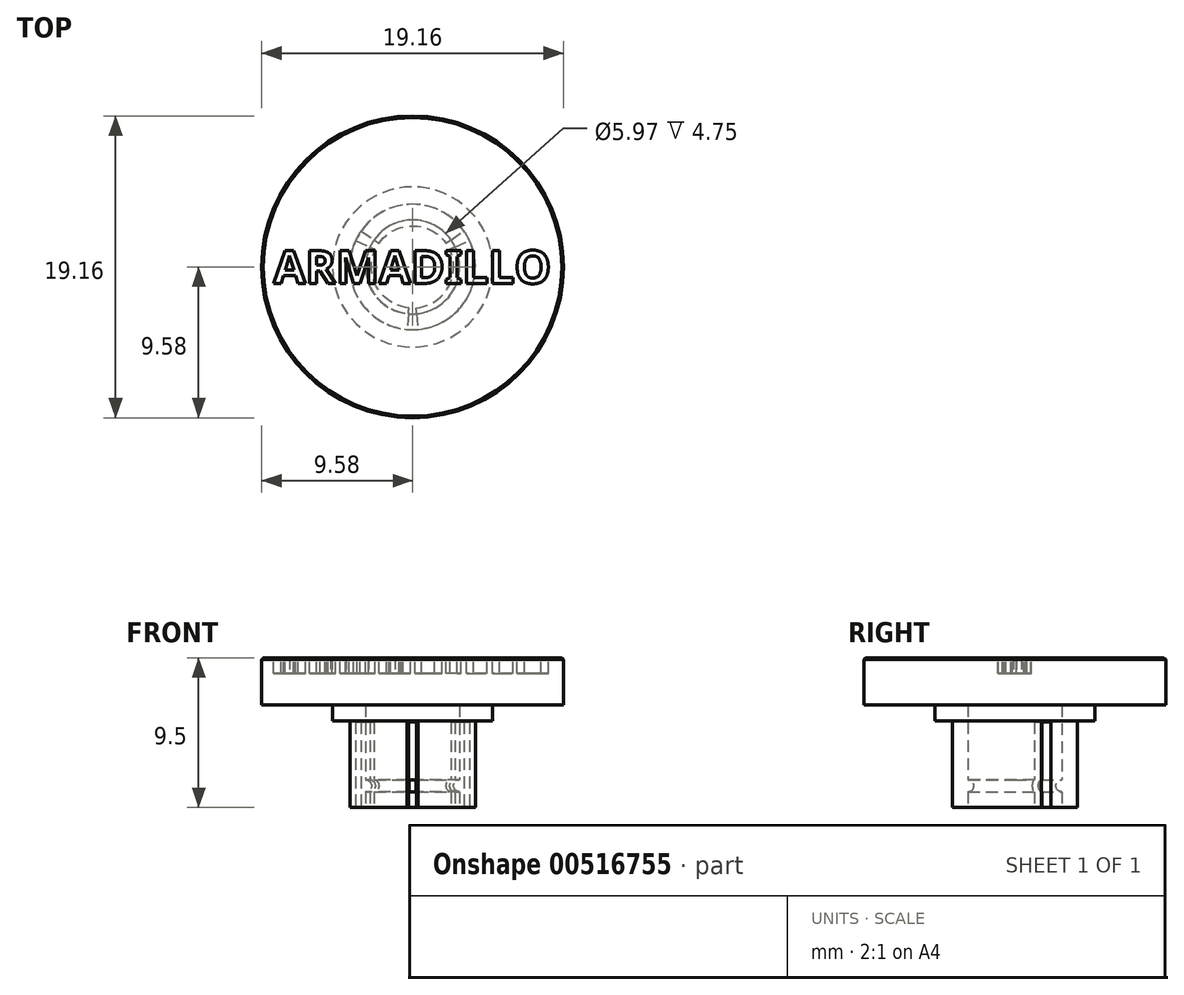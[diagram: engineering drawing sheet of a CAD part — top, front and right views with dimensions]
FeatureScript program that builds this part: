
annotation { "Feature Type Name" : "Feature", "Feature Type Description" : "" }
export const myFeature = defineFeature(function(context is Context, id is Id, definition is map)
    precondition{}
    {
        {
            var Q0;
            Q0=qCreatedBy(makeId("Front.planeOp"),FACE);
            var sketch = newSketch(context, id + "F0", { "sketchPlane" : qUnion([Q0])});
            skLineSegment(sketch, "E0", {"start": v(0, 6.5) * mm, "end": v(0, 9.5) * mm});
            skLineSegment(sketch, "E1", {"start": v(0, 9.5) * mm, "end": v(9.58, 9.5) * mm});
            skLineSegment(sketch, "E2", {"start": v(9.58, 9.5) * mm, "end": v(9.58, 6.5) * mm});
            skLineSegment(sketch, "E3", {"start": v(9.58, 6.5) * mm, "end": v(5.08, 6.5) * mm});
            skLineSegment(sketch, "E4", {"start": v(5.08, 6.5) * mm, "end": v(5.08, 5.5) * mm});
            skLineSegment(sketch, "E5", {"start": v(5.08, 5.5) * mm, "end": v(3.98, 5.5) * mm});
            skLineSegment(sketch, "E6", {"start": v(3.98, 5.5) * mm, "end": v(3.98, 0) * mm});
            skLineSegment(sketch, "E7", {"start": v(2.98, 6.5) * mm, "end": v(0, 6.5) * mm});
            skLineSegment(sketch, "E8", {"start": v(3.98, 0) * mm, "end": v(2.98, 0) * mm});
            skLineSegment(sketch, "E9", {"start": v(2.98, 0) * mm, "end": v(2.98, 1) * mm});
            skArc(sketch, "E10", {"start": v(2.98, 1.75) * mm, "mid": v(2.6, 1.37) * mm, "end": v(2.98, 1) * mm});
            skLineSegment(sketch, "E11.trimOffspring", {"start": v(2.98, 1.75) * mm, "end": v(2.98, 6.5) * mm});
            skSolve(sketch);
        }
        {
            var Q0;
            Q0=makeQuery(id+"F0.imprint","IMPRINT",FACE,{"disambiguationData":[TD([[makeQuery(id+"F0.imprint","IMPRINT",EDGE,{"derivedFrom":sQuery(id+"F0.wireOp",EDGE,"E0")}),-1.0]])]});
            var Q1;
            Q1=sQuery(id+"F0.wireOp",EDGE,"E0");
            revolve(context, id + "F1", {"entities" : qUnion([Q0]), "axis" : qUnion([Q1]), "revolveType" : RevolveType.FULL});
        }
        {
            var Q0;
            Q0=makeQuery(id+"F1.opRevolve","SWEPT_EDGE",EDGE,{"disambiguationData":[OSD([sQuery(id+"F0.wireOp",EDGE,"E1"),sQuery(id+"F0.wireOp",EDGE,"E2")])]});
            chamfer(context, id + "F2", {"entities" : qUnion([Q0]), "width" : 0.1 * mm, "tangentPropagation" : true});
        }
        {
            var Q0;
            Q0=makeQuery(id+"F1.opRevolve","SWEPT_FACE",FACE,{"disambiguationData":[OSD([sQuery(id+"F0.wireOp",EDGE,"E1")])]});
            var sketch = newSketch(context, id + "F3", { "sketchPlane" : qUnion([Q0])});
            skText(sketch, "E12", { "text": "ARMADILLO", "fontName": "NotoSans-Bold.ttf"});
            skPoint(sketch, "E13", {"position": v(0, 0) * mm});
            const initialGuessF3  = {"E12": [-0.00882, -0.00105, 1, 0, 0.0021]};
            skSetInitialGuess(sketch, initialGuessF3);
            skSolve(sketch);
        }
        {
            var Q0;
            Q0=qSketchRegion(id+"F3",true);
            extrude(context, id + "F4", {"entities" : qUnion([Q0]), "operationType" : NewBodyOperationType.REMOVE, "oppositeDirection" : true, "depth" : 1 * mm, "offsetDistance" : 25 * mm});
        }
        {
            var Q0;
            Q0=makeQuery(id+"F1.opRevolve","SWEPT_FACE",FACE,{"disambiguationData":[OSD([sQuery(id+"F0.wireOp",EDGE,"E8")])]});
            var sketch = newSketch(context, id + "F5", { "sketchPlane" : qUnion([Q0])});
            skCircle(sketch, "E14.0", {"center": v(0, 0) * mm, "radius": 3.98 * mm});
            skCircle(sketch, "E15.0", {"center": v(0, 0) * mm, "radius": 2.98 * mm});
            skLineSegment(sketch, "E16", {"start": v(-3.61, -1.68) * mm, "end": v(0, 0) * mm});
            skLineSegment(sketch, "E17", {"start": v(-3.26, -2.28) * mm, "end": v(0, 0) * mm});
            skLineSegment(sketch, "E18", {"start": v(0, 0) * mm, "end": v(-0.35, 3.97) * mm});
            skLineSegment(sketch, "E19", {"start": v(0, 0) * mm, "end": v(0.35, 3.97) * mm});
            skLineSegment(sketch, "E20", {"start": v(0, 0) * mm, "end": v(3.26, -2.28) * mm});
            skLineSegment(sketch, "E21", {"start": v(0, 0) * mm, "end": v(3.61, -1.68) * mm});
            skArc(sketch, "E22", {"start": v(-0.35, 3.97) * mm, "mid": v(0, 3.98) * mm, "end": v(0.35, 3.97) * mm});
            skLineSegment(sketch, "E23", {"start": v(0, 0) * mm, "end": v(0, 3.98) * mm, "construction": true});
            skSolve(sketch);
        }
        {
            var Q0;
            {var subQ0=sQuery(id+"F5.wireOp",EDGE,"E19");var subQ1=sQuery(id+"F5.wireOp",EDGE,"E15.0");var subQ2=makeQuery(id+"F5.imprint","INTERSECT",VERTEX,{"derivedFrom":[subQ1,subQ0]});Q0=makeQuery(id+"F5.imprint","IMPRINT",FACE,{"disambiguationData":[TD([[makeQuery(id+"F5.imprint","IMPRINT",EDGE,{"disambiguationData":[TD([[subQ2,-1.0]])],"derivedFrom":subQ1}),-1.0]])]});}
            var Q1;
            {var subQ0=sQuery(id+"F5.wireOp",EDGE,"E17");var subQ1=sQuery(id+"F5.wireOp",EDGE,"E15.0");var subQ2=makeQuery(id+"F5.imprint","INTERSECT",VERTEX,{"derivedFrom":[subQ1,subQ0]});Q1=makeQuery(id+"F5.imprint","IMPRINT",FACE,{"disambiguationData":[TD([[makeQuery(id+"F5.imprint","IMPRINT",EDGE,{"disambiguationData":[TD([[subQ2,1.0]])],"derivedFrom":subQ1}),-1.0]])]});}
            var Q2;
            {var subQ0=sQuery(id+"F5.wireOp",EDGE,"E20");var subQ1=sQuery(id+"F5.wireOp",EDGE,"E15.0");var subQ2=makeQuery(id+"F5.imprint","INTERSECT",VERTEX,{"derivedFrom":[subQ1,subQ0]});Q2=makeQuery(id+"F5.imprint","IMPRINT",FACE,{"disambiguationData":[TD([[makeQuery(id+"F5.imprint","IMPRINT",EDGE,{"disambiguationData":[TD([[subQ2,-1.0]])],"derivedFrom":subQ1}),-1.0]])]});}
            var Q3;
            {var subQ0=sQuery(id+"F5.wireOp",EDGE,"E19");var subQ1=sQuery(id+"F5.wireOp",EDGE,"E15.0");var subQ2=makeQuery(id+"F5.imprint","INTERSECT",VERTEX,{"derivedFrom":[subQ1,subQ0]});Q3=makeQuery(id+"F5.imprint","IMPRINT",FACE,{"disambiguationData":[TD([[makeQuery(id+"F5.imprint","IMPRINT",EDGE,{"disambiguationData":[TD([[subQ2,-1.0]])],"derivedFrom":subQ1}),1.0]])]});}
            var Q4;
            {var subQ0=sQuery(id+"F5.wireOp",EDGE,"E20");var subQ1=sQuery(id+"F5.wireOp",EDGE,"E15.0");var subQ2=makeQuery(id+"F5.imprint","INTERSECT",VERTEX,{"derivedFrom":[subQ1,subQ0]});Q4=makeQuery(id+"F5.imprint","IMPRINT",FACE,{"disambiguationData":[TD([[makeQuery(id+"F5.imprint","IMPRINT",EDGE,{"disambiguationData":[TD([[subQ2,-1.0]])],"derivedFrom":subQ1}),1.0]])]});}
            var Q5;
            {var subQ0=sQuery(id+"F5.wireOp",EDGE,"E17");var subQ1=sQuery(id+"F5.wireOp",EDGE,"E15.0");var subQ2=makeQuery(id+"F5.imprint","INTERSECT",VERTEX,{"derivedFrom":[subQ1,subQ0]});Q5=makeQuery(id+"F5.imprint","IMPRINT",FACE,{"disambiguationData":[TD([[makeQuery(id+"F5.imprint","IMPRINT",EDGE,{"disambiguationData":[TD([[subQ2,1.0]])],"derivedFrom":subQ1}),1.0]])]});}
            var Q6;
            Q6=makeQuery(id+"F1.opRevolve","SWEPT_FACE",FACE,{"disambiguationData":[OSD([sQuery(id+"F0.wireOp",EDGE,"E5")])]});
            extrude(context, id + "F6", {"entities" : qUnion([Q0, Q1, Q2, Q3, Q4, Q5]), "operationType" : NewBodyOperationType.REMOVE, "oppositeDirection" : true, "depth" : 5.42 * mm, "offsetDistance" : 25 * mm});
        }
    });
